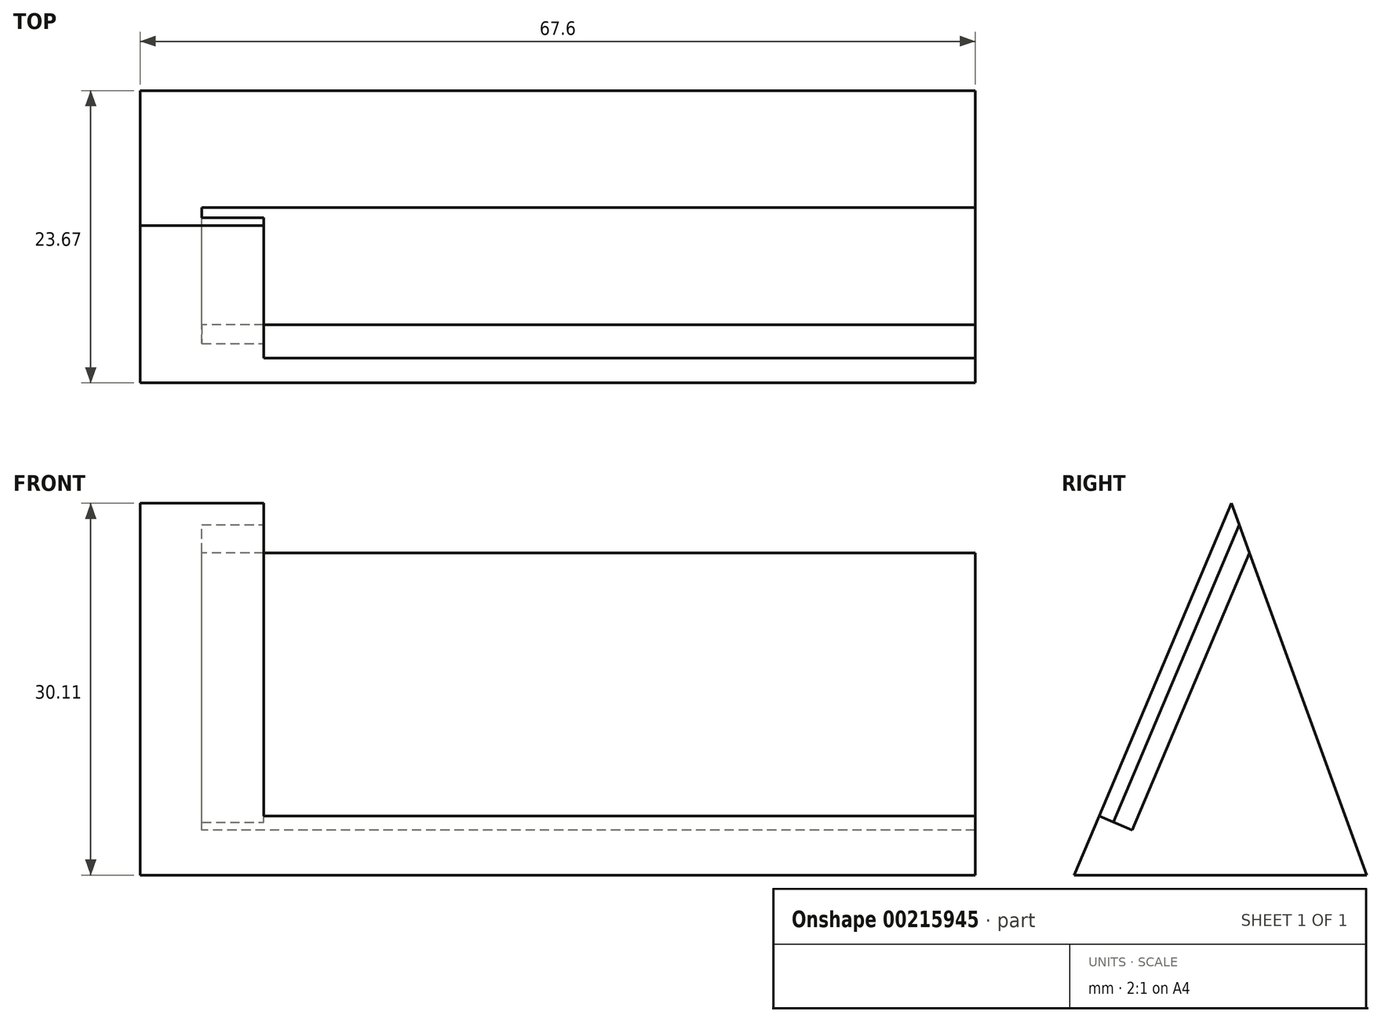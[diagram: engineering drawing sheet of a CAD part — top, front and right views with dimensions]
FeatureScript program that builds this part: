
annotation { "Feature Type Name" : "Feature", "Feature Type Description" : "" }
export const myFeature = defineFeature(function(context is Context, id is Id, definition is map)
    precondition{}
    {
        {
            var Q0;
            Q0=qCreatedBy(makeId("Right.planeOp"),FACE);
            var sketch = newSketch(context, id + "F0", { "sketchPlane" : qUnion([Q0])});
            skLineSegment(sketch, "E0", {"start": v(0, 0) * mm, "end": v(11.03, 26.08) * mm});
            skLineSegment(sketch, "E1", {"start": v(11.03, 26.08) * mm, "end": v(20.5, 0) * mm});
            skLineSegment(sketch, "E2", {"start": v(20.5, 0) * mm, "end": v(0, 0) * mm});
            skLineSegment(sketch, "E3", {"start": v(1.54, 3.63) * mm, "end": v(0, 4.28) * mm});
            skLineSegment(sketch, "E4", {"start": v(0, 4.28) * mm, "end": v(0, 0) * mm});
            skLineSegment(sketch, "E5", {"start": v(0, 4.28) * mm, "end": v(-1.81, 0) * mm});
            skLineSegment(sketch, "E6", {"start": v(-1.81, 0) * mm, "end": v(0, 0) * mm});
            skLineSegment(sketch, "E7", {"start": v(-1.81, 0) * mm, "end": v(9.47, 26.67) * mm});
            skLineSegment(sketch, "E8", {"start": v(8.31, 27.15) * mm, "end": v(-3.17, 0) * mm});
            skLineSegment(sketch, "E9", {"start": v(-3.17, 0) * mm, "end": v(-1.81, 0) * mm});
            skLineSegment(sketch, "E10", {"start": v(8.31, 27.15) * mm, "end": v(9.57, 30.11) * mm});
            skLineSegment(sketch, "E11", {"start": v(11.03, 26.08) * mm, "end": v(9.57, 30.11) * mm});
            skLineSegment(sketch, "E12", {"start": v(9.47, 26.67) * mm, "end": v(10.2, 28.39) * mm});
            skLineSegment(sketch, "E13", {"start": v(0, 4.28) * mm, "end": v(-1.15, 4.77) * mm});
            skLineSegment(sketch, "E14", {"start": v(20.5, 0) * mm, "end": v(20.5, 30.11) * mm});
            skLineSegment(sketch, "E15", {"start": v(20.5, 30.11) * mm, "end": v(9.57, 30.11) * mm});
            skSolve(sketch);
        }
        {
            var Q0;
            Q0=makeQuery(id+"F0.imprint","IMPRINT",FACE,{"disambiguationData":[TD([[makeQuery(id+"F0.imprint","IMPRINT",EDGE,{"derivedFrom":sQuery(id+"F0.wireOp",EDGE,"E0")}),-1.0]])]});
            var Q1;
            {var subQ2=sQuery(id+"F0.wireOp",EDGE,"E3");Q1=makeQuery(id+"F0.imprint","IMPRINT",FACE,{"disambiguationData":[TD([[makeQuery(id+"F0.imprint","IMPRINT",EDGE,{"derivedFrom":subQ2}),1.0]])]});}
            var Q2;
            Q2=makeQuery(id+"F0.imprint","IMPRINT",FACE,{"disambiguationData":[TD([[makeQuery(id+"F0.imprint","IMPRINT",EDGE,{"derivedFrom":sQuery(id+"F0.wireOp",EDGE,"E4")}),-1.0]])]});
            var Q3;
            {var subQ0=sQuery(id+"F0.wireOp",EDGE,"dQav16My-iky8-KVIo-PDfP-vxpZZ8rctp8x");Q3=makeQuery(id+"F0.imprint","IMPRINT",FACE,{"disambiguationData":[TD([[makeQuery(id+"F0.imprint","IMPRINT",EDGE,{"derivedFrom":subQ0}),1.0]])]});}
            var Q4;
            {var subQ2=sQuery(id+"F0.wireOp",EDGE,"E9");Q4=makeQuery(id+"F0.imprint","IMPRINT",FACE,{"disambiguationData":[TD([[makeQuery(id+"F0.imprint","IMPRINT",EDGE,{"derivedFrom":subQ2}),1.0]])]});}
            extrude(context, id + "F1", {"entities" : qUnion([Q0, Q1, Q2, Q3, Q4]), "depth" : 57.6 * mm});
        }
        {
            var Q0;
            {var subQ0=sQuery(id+"F0.wireOp",EDGE,"E10");Q0=makeQuery(id+"F0.imprint","IMPRINT",FACE,{"disambiguationData":[TD([[makeQuery(id+"F0.imprint","IMPRINT",EDGE,{"derivedFrom":subQ0}),-1.0]])]});}
            var Q1;
            {var subQ3=sQuery(id+"F0.wireOp",EDGE,"E1");Q1=makeQuery(id+"F0.imprint","IMPRINT",FACE,{"disambiguationData":[TD([[makeQuery(id+"F0.imprint","IMPRINT",EDGE,{"derivedFrom":subQ3}),-1.0]])]});}
            var Q2;
            {var subQ0=sQuery(id+"F0.wireOp",EDGE,"E4");Q2=makeQuery(id+"F0.imprint","IMPRINT",FACE,{"disambiguationData":[TD([[makeQuery(id+"F0.imprint","IMPRINT",EDGE,{"derivedFrom":subQ0}),-1.0]])]});}
            var Q3;
            {var subQ2=sQuery(id+"F0.wireOp",EDGE,"E9");Q3=makeQuery(id+"F0.imprint","IMPRINT",FACE,{"disambiguationData":[TD([[makeQuery(id+"F0.imprint","IMPRINT",EDGE,{"derivedFrom":subQ2}),1.0]])]});}
            var Q4;
            {var subQ2=sQuery(id+"F0.wireOp",EDGE,"E3");Q4=makeQuery(id+"F0.imprint","IMPRINT",FACE,{"disambiguationData":[TD([[makeQuery(id+"F0.imprint","IMPRINT",EDGE,{"derivedFrom":subQ2}),1.0]])]});}
            extrude(context, id + "F2", {"entities" : qUnion([Q0, Q1, Q2, Q3, Q4]), "operationType" : NewBodyOperationType.ADD, "oppositeDirection" : true, "depth" : 5 * mm});
        }
        {
            var Q0;
            {var subQ0=sQuery(id+"F0.wireOp",EDGE,"E10");Q0=makeQuery(id+"F0.imprint","IMPRINT",FACE,{"disambiguationData":[TD([[makeQuery(id+"F0.imprint","IMPRINT",EDGE,{"derivedFrom":subQ0}),-1.0]])]});}
            var Q1;
            {var subQ5=sQuery(id+"F0.wireOp",EDGE,"E3");Q1=makeQuery(id+"F0.imprint","IMPRINT",FACE,{"disambiguationData":[TD([[makeQuery(id+"F0.imprint","IMPRINT",EDGE,{"derivedFrom":subQ5}),-1.0]])]});}
            var Q2;
            {var subQ3=sQuery(id+"F0.wireOp",EDGE,"E1");Q2=makeQuery(id+"F0.imprint","IMPRINT",FACE,{"disambiguationData":[TD([[makeQuery(id+"F0.imprint","IMPRINT",EDGE,{"derivedFrom":subQ3}),-1.0]])]});}
            var Q3;
            {var subQ2=sQuery(id+"F0.wireOp",EDGE,"E3");Q3=makeQuery(id+"F0.imprint","IMPRINT",FACE,{"disambiguationData":[TD([[makeQuery(id+"F0.imprint","IMPRINT",EDGE,{"derivedFrom":subQ2}),1.0]])]});}
            var Q4;
            {var subQ0=sQuery(id+"F0.wireOp",EDGE,"E4");Q4=makeQuery(id+"F0.imprint","IMPRINT",FACE,{"disambiguationData":[TD([[makeQuery(id+"F0.imprint","IMPRINT",EDGE,{"derivedFrom":subQ0}),-1.0]])]});}
            var Q5;
            {var subQ2=sQuery(id+"F0.wireOp",EDGE,"E9");Q5=makeQuery(id+"F0.imprint","IMPRINT",FACE,{"disambiguationData":[TD([[makeQuery(id+"F0.imprint","IMPRINT",EDGE,{"derivedFrom":subQ2}),1.0]])]});}
            extrude(context, id + "F3", {"entities" : qUnion([Q0, Q1, Q2, Q3, Q4, Q5]), "operationType" : NewBodyOperationType.ADD, "oppositeDirection" : true, "depth" : 10 * mm, "hasSecondDirection" : true, "secondDirectionOppositeDirection" : true, "secondDirectionDepth" : 5 * mm});
        }
    });
